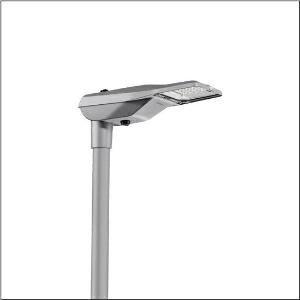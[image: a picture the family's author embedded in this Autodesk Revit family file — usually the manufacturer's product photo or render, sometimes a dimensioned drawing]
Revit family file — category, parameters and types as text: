
# Revit family: streetlight_sl_21_iq_micro___st0_8a_5xe1c31y08cb_ba99
name_source: partatom
category: Lighting Fixtures
units: mm (PartAtom-declared; Revit-internal decimal feet)

## family parameters
Cut with Voids When Loaded = No
Host = Face
Light Source = No
Part Type = Normal
Room Calculation Point = No
Round Connector Dimension = Use Diameter
Shared = No

## types (1)
- --- (1 x LED, 2880 lm, 19.1 W, 3000K)
    Apparent Load = 19 VA
    CIE Flux Codes = 38 75 97 100 100
    Color Rendering = 70
    Color Temperature = 3000K
    Default Elevation = 1800 mm
    Description = Streetlight SL 21 iQ micro, mast luminaire, primary light control with lens, of PMMA, primary optical cover: cover, of toughened safety glass, transparent, light distribution: ST0.8a, light emission: direct distribution, primary light characteristic: asymmetric, installation type: post-top, side-entry, LED, High Power LED, rated luminous flux: 2.880lm, luminous efficacy: 151lm/W, light colour: 730, colour temperature: 3000K, control: presetting dimming logarithmic, Street-Remote, Auto-Match, Temp-Guard, Lumen-Switch, Night-Set, Smart-Wire, Light-Fading, Desk-Remote (wireless, voltage-free reading and setting of iQ features in the workshop via application-optimized NFC function/RFID function), optimised constant luminous flux control (CLO 2.0), mains connection: 220..240V, AC, 50/60Hz, start of lifetime: 19W, end of service life: 20W, reduction: 9W, luminaire housing, of diecast aluminium, powder-coated, Siteco® metallic grey (DB 702S), corrosivity category C5 mid according to DIN EN ISO 12944, please order mast flange separately, inclination adjustable: 0°, 5°, 10°, 15°, sealing non-destructively replaceable, multi-level sealing system, length: 528mm, width: 235mm, height: 110mm, mast flange for spigot size: 42mm (side-entry): 5XC10008XM4, 60/48mm (side-entry/post-top): 5XC10108XM2, 76/60mm (side-entry/post-top): 5XC10108XM1, Smart Interface below and above, protection rating (complete): IP66, insulation class (complete): insulation class II (safety insulation), certification: CE, ENEC, ENEC+, VDE, impact resistance: IK09, permissible operating ambient temperature for outdoor applications: -40..+50°C, standard-compliant lighting for roads and squares, packaging unit: 1 piece

Light Distribution: ST0.8a
    Height = 110 mm
    Lamp = 1 x LED
    Lamp Light Flux = 2880 lm
    Lamp Power = 19.1 W
    Lamp count = 1
    Length = 528 mm
    Luminous efficacy = 151 lm/W
    Manufacturer = Siteco
    ModVariant = No
    Model = 5XE1C31Y08CB
    Number of Poles = 1
    OnlyDefault = Yes
    Power Factor = 1
    Product Name = Streetlight SL 21 iQ micro | ST0.8a
    Product group = mast luminaire | pylon top
    ProductGroupID = 6100
    Protection Class = Protection class II
    Protection Degree = IP 66
    RLX_Detail_Level = 1
    RLX_Emergency_Light_Flux = 0 lm
    RLX_Emergency_Type = 0
    RLX_Emergency_Type_DB = No
    RlxData = <blob elided: 98337 chars, md5=186cb26a>
    Socket = socket
    Standby Power = 0 W
    System Light Flux = 2880 lm
    System Power = 19 W
    Type Comments = factory setting: luminous flux: 100 % | dim-lin: 254 | 387 mA
    Type Image = l_1007239.jpg
    URL = http://relux.com
    VarID = @adj_043463
    Voltage = 0 V
    Weight = 0.00 kg
    Width = 235 mm

## geometry (parser evidence)
native form markers: Blend x4, Sweep x10
no freeform markers — native parametric forms only
